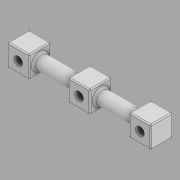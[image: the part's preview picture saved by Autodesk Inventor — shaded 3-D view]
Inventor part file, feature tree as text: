
AUTODESK INVENTOR PART (.ipt)
format: ipt  version: 2020 (Build 240168000, 168)  size: 203,264 bytes
history: native  units: mm
features: extrude x5, sketch x5, fillet x2, other x1
ambient origin geometry x8: Origin, YZ Plane, XZ Plane, XY Plane, X Axis, Y Axis, Z Axis, Center Point
bodies: Body1 (feature_tree)
feature tree (13):
  other  "Sólido1"
  extrude  "Extrusión1"  Depth=10.0mm
  extrude  "Extrusión2"  Depth=10.0mm TaperAngle=0.0deg
  extrude  "Extrusión3"  Depth=18.0mm TaperAngle=0.0deg
  extrude  "Extrusión4"  Depth=10.0mm
  extrude  "Extrusión5"  Depth=4.0mm
  fillet  "Empalme1"  Radius=10.0mm
  fillet  "Empalme2"  Radius=6.0mm
  sketch  "Boceto1"  dims[d0=10.0mm d1=10.0mm]
  sketch  "Boceto2"  dims[d2=4.0mm d3=10.0mm d4=0.0mm]
  sketch  "Boceto3"  dims[d5=6.0mm d6=18.0mm d7=0.0mm]
  sketch  "Boceto4"  dims[d8=10.0mm d9=10.0mm]
  sketch  "Boceto5"  dims[d10=28.0mm d11=4.0mm d12=10.0mm d13=0.0mm d14=6.0mm d15=18.0mm d16=0.0mm d17=10.0mm d18=10.0mm d19=28.0mm d20=4.0mm d21=10.0mm d22=0.0mm d23=1.0mm d24=0.5mm]
